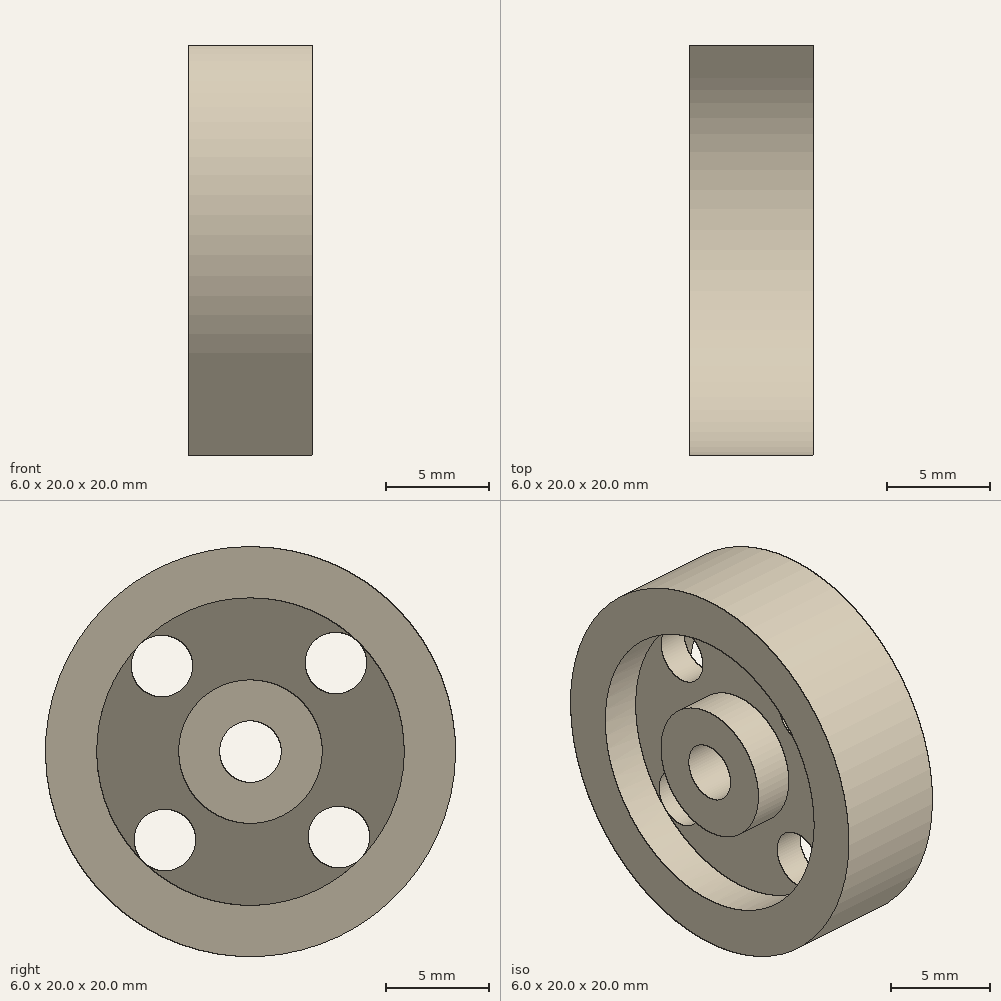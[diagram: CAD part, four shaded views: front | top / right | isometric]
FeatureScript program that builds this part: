
annotation { "Feature Type Name" : "Feature", "Feature Type Description" : "" }
export const myFeature = defineFeature(function(context is Context, id is Id, definition is map)
    precondition{}
    {
        {
            var Q0;
            Q0=qCreatedBy(makeId("Top.planeOp"),FACE);
            var sketch = newSketch(context, id + "F0", { "sketchPlane" : qUnion([Q0])});
            skLineSegment(sketch, "E0", {"start": v(9.5, -46.1) * mm, "end": v(25.4, -46.1) * mm});
            skLineSegment(sketch, "E1", {"start": v(11.37, -46.1) * mm, "end": v(11.37, -44.6) * mm});
            skLineSegment(sketch, "E2.bottom", {"start": v(12.58, -42.6) * mm, "end": v(14.21, -42.6) * mm});
            skLineSegment(sketch, "E2.top", {"start": v(12.58, -38.6) * mm, "end": v(14.21, -38.6) * mm});
            skLineSegment(sketch, "E2.left", {"start": v(12.58, -42.6) * mm, "end": v(12.58, -38.6) * mm});
            skLineSegment(sketch, "E2.right", {"start": v(14.21, -42.6) * mm, "end": v(14.21, -38.6) * mm});
            skLineSegment(sketch, "E3.bottom", {"start": v(13.4, -42.6) * mm, "end": v(10.4, -42.6) * mm});
            skLineSegment(sketch, "E3.top", {"start": v(13.4, -44.6) * mm, "end": v(10.4, -44.6) * mm});
            skLineSegment(sketch, "E3.left", {"start": v(13.4, -42.6) * mm, "end": v(13.4, -44.6) * mm});
            skLineSegment(sketch, "E3.right", {"start": v(10.4, -42.6) * mm, "end": v(10.4, -44.6) * mm});
            skLineSegment(sketch, "E4.bottom", {"start": v(13.4, -42.6) * mm, "end": v(16.4, -42.6) * mm});
            skLineSegment(sketch, "E4.top", {"start": v(13.4, -44.6) * mm, "end": v(16.4, -44.6) * mm});
            skLineSegment(sketch, "E4.right", {"start": v(16.4, -42.6) * mm, "end": v(16.4, -44.6) * mm});
            skLineSegment(sketch, "E5.bottom", {"start": v(13.4, -38.6) * mm, "end": v(10.4, -38.6) * mm});
            skLineSegment(sketch, "E5.top", {"start": v(13.4, -36.1) * mm, "end": v(10.4, -36.1) * mm});
            skLineSegment(sketch, "E5.left", {"start": v(13.4, -38.6) * mm, "end": v(13.4, -36.1) * mm});
            skLineSegment(sketch, "E5.right", {"start": v(10.4, -38.6) * mm, "end": v(10.4, -36.1) * mm});
            skLineSegment(sketch, "E6.bottom", {"start": v(13.4, -38.6) * mm, "end": v(16.4, -38.6) * mm});
            skLineSegment(sketch, "E6.top", {"start": v(13.4, -36.1) * mm, "end": v(16.4, -36.1) * mm});
            skLineSegment(sketch, "E6.right", {"start": v(16.4, -38.6) * mm, "end": v(16.4, -36.1) * mm});
            skSolve(sketch);
        }
        {
            var Q0;
            Q0 = qSketchRegion(id + "F0", true);
            var Q1;
            Q1=sQuery(id+"F0.wireOp",EDGE,"E0");
            revolve(context, id + "F1", {"entities" : qUnion([Q0]), "axis" : qUnion([Q1]), "revolveType" : RevolveType.FULL});
        }
        {
            var Q0;
            Q0=makeQuery(id+"F1.opRevolve","SWEPT_FACE",FACE,{"disambiguationData":[OSD([sQuery(id+"F0.wireOp",EDGE,"E2.right")])]});
            var sketch = newSketch(context, id + "F2", { "sketchPlane" : qUnion([Q0])});
            skLineSegment(sketch, "E7", {"start": v(-48.62, 2.43) * mm, "end": v(-50.42, 4.17) * mm});
            skCircle(sketch, "E8", {"center": v(-50.42, 4.17) * mm, "radius": 1.5 * mm});
            skCircle(sketch, "E9.1.0", {"center": v(-50.28, -4.31) * mm, "radius": 1.5 * mm});
            skCircle(sketch, "E9.2.0", {"center": v(-41.8, -4.17) * mm, "radius": 1.5 * mm});
            skCircle(sketch, "E9.3.0", {"center": v(-41.94, 4.31) * mm, "radius": 1.5 * mm});
            skPoint(sketch, "E9.center", {"position": v(-46.1, 0) * mm});
            skSolve(sketch);
        }
        {
            var Q0;
            Q0 = qSketchRegion(id + "F2", true);
            extrude(context, id + "F3", {"entities" : qUnion([Q0]), "operationType" : NewBodyOperationType.REMOVE, "endBound" : BoundingType.THROUGH_ALL, "oppositeDirection" : true, "depth" : 25 * mm});
        }
    });
